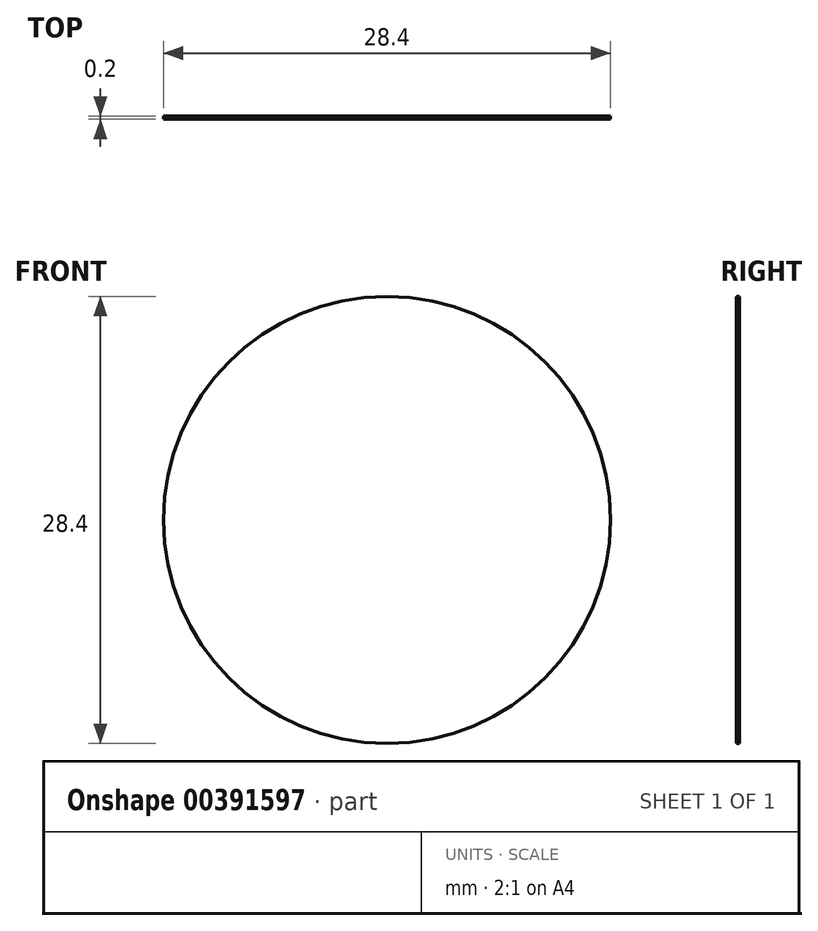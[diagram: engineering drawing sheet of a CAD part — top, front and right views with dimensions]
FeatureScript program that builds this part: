
annotation { "Feature Type Name" : "Feature", "Feature Type Description" : "" }
export const myFeature = defineFeature(function(context is Context, id is Id, definition is map)
    precondition{}
    {
        {
            var Q0;
            Q0=qCreatedBy(makeId("Front.planeOp"),FACE);
            var sketch = newSketch(context, id + "F0", { "sketchPlane" : qUnion([Q0])});
            skCircle(sketch, "E0", {"center": v(0, 0) * mm, "radius": 7 * mm, "construction": true});
            skCircle(sketch, "E1", {"center": v(0, 0) * mm, "radius": 10.5 * mm, "construction": true});
            skLineSegment(sketch, "E2", {"start": v(0, 7) * mm, "end": v(0.75, 7) * mm, "construction": true});
            skLineSegment(sketch, "E3", {"start": v(0.75, 7) * mm, "end": v(0.75, 13.5) * mm, "construction": true});
            skLineSegment(sketch, "E4", {"start": v(0.75, 13.5) * mm, "end": v(0, 13.5) * mm, "construction": true});
            skLineSegment(sketch, "E5", {"start": v(0, 13.5) * mm, "end": v(-0.75, 13.5) * mm, "construction": true});
            skLineSegment(sketch, "E6", {"start": v(-0.75, 13.5) * mm, "end": v(-0.75, 7) * mm, "construction": true});
            skLineSegment(sketch, "E7", {"start": v(-0.75, 7) * mm, "end": v(0, 7) * mm, "construction": true});
            skLineSegment(sketch, "E8.1.0", {"start": v(-2.85, 6.44) * mm, "end": v(-6.1, 12.07) * mm});
            skLineSegment(sketch, "E8.1.1", {"start": v(-7.4, 11.32) * mm, "end": v(-4.15, 5.69) * mm});
            skLineSegment(sketch, "E8.1.2", {"start": v(-4.15, 5.69) * mm, "end": v(-3.5, 6.06) * mm});
            skLineSegment(sketch, "E8.1.3", {"start": v(-3.5, 6.06) * mm, "end": v(-2.85, 6.44) * mm});
            skLineSegment(sketch, "E8.1.4", {"start": v(-6.1, 12.07) * mm, "end": v(-6.75, 11.7) * mm});
            skLineSegment(sketch, "E8.1.5", {"start": v(-6.75, 11.7) * mm, "end": v(-7.4, 11.32) * mm});
            skLineSegment(sketch, "E8.2.0", {"start": v(-5.69, 4.15) * mm, "end": v(-11.32, 7.4) * mm});
            skLineSegment(sketch, "E8.2.1", {"start": v(-12.07, 6.1) * mm, "end": v(-6.44, 2.85) * mm});
            skLineSegment(sketch, "E8.2.2", {"start": v(-6.44, 2.85) * mm, "end": v(-6.06, 3.5) * mm});
            skLineSegment(sketch, "E8.2.3", {"start": v(-6.06, 3.5) * mm, "end": v(-5.69, 4.15) * mm});
            skLineSegment(sketch, "E8.2.4", {"start": v(-11.32, 7.4) * mm, "end": v(-11.7, 6.75) * mm});
            skLineSegment(sketch, "E8.2.5", {"start": v(-11.7, 6.75) * mm, "end": v(-12.07, 6.1) * mm});
            skLineSegment(sketch, "E8.3.0", {"start": v(-7, 0.75) * mm, "end": v(-13.5, 0.75) * mm, "construction": true});
            skLineSegment(sketch, "E8.3.1", {"start": v(-13.5, -0.75) * mm, "end": v(-7, -0.75) * mm, "construction": true});
            skLineSegment(sketch, "E8.3.2", {"start": v(-7, -0.75) * mm, "end": v(-7, 0) * mm, "construction": true});
            skLineSegment(sketch, "E8.3.3", {"start": v(-7, 0) * mm, "end": v(-7, 0.75) * mm, "construction": true});
            skLineSegment(sketch, "E8.3.4", {"start": v(-13.5, 0.75) * mm, "end": v(-13.5, 0) * mm, "construction": true});
            skLineSegment(sketch, "E8.3.5", {"start": v(-13.5, 0) * mm, "end": v(-13.5, -0.75) * mm, "construction": true});
            skLineSegment(sketch, "E8.4.0", {"start": v(-6.44, -2.85) * mm, "end": v(-12.07, -6.1) * mm});
            skLineSegment(sketch, "E8.4.1", {"start": v(-11.32, -7.4) * mm, "end": v(-5.69, -4.15) * mm});
            skLineSegment(sketch, "E8.4.2", {"start": v(-5.69, -4.15) * mm, "end": v(-6.06, -3.5) * mm});
            skLineSegment(sketch, "E8.4.3", {"start": v(-6.06, -3.5) * mm, "end": v(-6.44, -2.85) * mm});
            skLineSegment(sketch, "E8.4.4", {"start": v(-12.07, -6.1) * mm, "end": v(-11.7, -6.75) * mm});
            skLineSegment(sketch, "E8.4.5", {"start": v(-11.7, -6.75) * mm, "end": v(-11.32, -7.4) * mm});
            skLineSegment(sketch, "E8.5.0", {"start": v(-4.15, -5.69) * mm, "end": v(-7.4, -11.32) * mm});
            skLineSegment(sketch, "E8.5.1", {"start": v(-6.1, -12.07) * mm, "end": v(-2.85, -6.44) * mm});
            skLineSegment(sketch, "E8.5.2", {"start": v(-2.85, -6.44) * mm, "end": v(-3.5, -6.06) * mm});
            skLineSegment(sketch, "E8.5.3", {"start": v(-3.5, -6.06) * mm, "end": v(-4.15, -5.69) * mm});
            skLineSegment(sketch, "E8.5.4", {"start": v(-7.4, -11.32) * mm, "end": v(-6.75, -11.7) * mm});
            skLineSegment(sketch, "E8.5.5", {"start": v(-6.75, -11.7) * mm, "end": v(-6.1, -12.07) * mm});
            skLineSegment(sketch, "E8.6.0", {"start": v(-0.75, -7) * mm, "end": v(-0.75, -13.5) * mm, "construction": true});
            skLineSegment(sketch, "E8.6.1", {"start": v(0.75, -13.5) * mm, "end": v(0.75, -7) * mm, "construction": true});
            skLineSegment(sketch, "E8.6.2", {"start": v(0.75, -7) * mm, "end": v(0, -7) * mm, "construction": true});
            skLineSegment(sketch, "E8.6.3", {"start": v(0, -7) * mm, "end": v(-0.75, -7) * mm, "construction": true});
            skLineSegment(sketch, "E8.6.4", {"start": v(-0.75, -13.5) * mm, "end": v(0, -13.5) * mm, "construction": true});
            skLineSegment(sketch, "E8.6.5", {"start": v(0, -13.5) * mm, "end": v(0.75, -13.5) * mm, "construction": true});
            skLineSegment(sketch, "E8.7.0", {"start": v(2.85, -6.44) * mm, "end": v(6.1, -12.07) * mm});
            skLineSegment(sketch, "E8.7.1", {"start": v(7.4, -11.32) * mm, "end": v(4.15, -5.69) * mm});
            skLineSegment(sketch, "E8.7.2", {"start": v(4.15, -5.69) * mm, "end": v(3.5, -6.06) * mm});
            skLineSegment(sketch, "E8.7.3", {"start": v(3.5, -6.06) * mm, "end": v(2.85, -6.44) * mm});
            skLineSegment(sketch, "E8.7.4", {"start": v(6.1, -12.07) * mm, "end": v(6.75, -11.7) * mm});
            skLineSegment(sketch, "E8.7.5", {"start": v(6.75, -11.7) * mm, "end": v(7.4, -11.32) * mm});
            skLineSegment(sketch, "E8.8.0", {"start": v(5.69, -4.15) * mm, "end": v(11.32, -7.4) * mm});
            skLineSegment(sketch, "E8.8.1", {"start": v(12.07, -6.1) * mm, "end": v(6.44, -2.85) * mm});
            skLineSegment(sketch, "E8.8.2", {"start": v(6.44, -2.85) * mm, "end": v(6.06, -3.5) * mm});
            skLineSegment(sketch, "E8.8.3", {"start": v(6.06, -3.5) * mm, "end": v(5.69, -4.15) * mm});
            skLineSegment(sketch, "E8.8.4", {"start": v(11.32, -7.4) * mm, "end": v(11.7, -6.75) * mm});
            skLineSegment(sketch, "E8.8.5", {"start": v(11.7, -6.75) * mm, "end": v(12.07, -6.1) * mm});
            skLineSegment(sketch, "E8.9.0", {"start": v(7, -0.75) * mm, "end": v(13.5, -0.75) * mm, "construction": true});
            skLineSegment(sketch, "E8.9.1", {"start": v(13.5, 0.75) * mm, "end": v(7, 0.75) * mm, "construction": true});
            skLineSegment(sketch, "E8.9.2", {"start": v(7, 0.75) * mm, "end": v(7, 0) * mm, "construction": true});
            skLineSegment(sketch, "E8.9.3", {"start": v(7, 0) * mm, "end": v(7, -0.75) * mm, "construction": true});
            skLineSegment(sketch, "E8.9.4", {"start": v(13.5, -0.75) * mm, "end": v(13.5, 0) * mm, "construction": true});
            skLineSegment(sketch, "E8.9.5", {"start": v(13.5, 0) * mm, "end": v(13.5, 0.75) * mm, "construction": true});
            skLineSegment(sketch, "E8.10.0", {"start": v(6.44, 2.85) * mm, "end": v(12.07, 6.1) * mm});
            skLineSegment(sketch, "E8.10.1", {"start": v(11.32, 7.4) * mm, "end": v(5.69, 4.15) * mm});
            skLineSegment(sketch, "E8.10.2", {"start": v(5.69, 4.15) * mm, "end": v(6.06, 3.5) * mm});
            skLineSegment(sketch, "E8.10.3", {"start": v(6.06, 3.5) * mm, "end": v(6.44, 2.85) * mm});
            skLineSegment(sketch, "E8.10.4", {"start": v(12.07, 6.1) * mm, "end": v(11.7, 6.75) * mm});
            skLineSegment(sketch, "E8.10.5", {"start": v(11.7, 6.75) * mm, "end": v(11.32, 7.4) * mm});
            skLineSegment(sketch, "E8.11.0", {"start": v(4.15, 5.69) * mm, "end": v(7.4, 11.32) * mm});
            skLineSegment(sketch, "E8.11.1", {"start": v(6.1, 12.07) * mm, "end": v(2.85, 6.44) * mm});
            skLineSegment(sketch, "E8.11.2", {"start": v(2.85, 6.44) * mm, "end": v(3.5, 6.06) * mm});
            skLineSegment(sketch, "E8.11.3", {"start": v(3.5, 6.06) * mm, "end": v(4.15, 5.69) * mm});
            skLineSegment(sketch, "E8.11.4", {"start": v(7.4, 11.32) * mm, "end": v(6.75, 11.7) * mm});
            skLineSegment(sketch, "E8.11.5", {"start": v(6.75, 11.7) * mm, "end": v(6.1, 12.07) * mm});
            skCircle(sketch, "E9", {"center": v(0, 0) * mm, "radius": 13.5 * mm, "construction": true});
            skSolve(sketch);
        }
        {
            var Q0;
            Q0=qCreatedBy(makeId("Front.planeOp"),FACE);
            var sketch = newSketch(context, id + "F1", { "sketchPlane" : qUnion([Q0])});
            skText(sketch, "E10", { "text": "12", "fontName": "AllertaStencil-Regular.ttf"});
            skText(sketch, "E11", { "text": "6", "fontName": "AllertaStencil-Regular.ttf"});
            skText(sketch, "E12", { "text": "9", "fontName": "AllertaStencil-Regular.ttf"});
            skPoint(sketch, "E13", {"position": v(-10.5, 0) * mm});
            skText(sketch, "E14", { "text": "3", "fontName": "AllertaStencil-Regular.ttf"});
            skCircle(sketch, "E15", {"center": v(0, 0) * mm, "radius": 10.5 * mm, "construction": true});
            skCircle(sketch, "E16", {"center": v(0, 0) * mm, "radius": 7 * mm, "construction": true});
            skLineSegment(sketch, "E17", {"start": v(0, 0) * mm, "end": v(0, 10.5) * mm, "construction": true});
            skLineSegment(sketch, "E18.1.0", {"start": v(0, 0) * mm, "end": v(-10.5, 0) * mm, "construction": true});
            skLineSegment(sketch, "E18.2.0", {"start": v(0, 0) * mm, "end": v(0, -10.5) * mm, "construction": true});
            skLineSegment(sketch, "E18.3.0", {"start": v(0, 0) * mm, "end": v(10.5, 0) * mm, "construction": true});
            skPoint(sketch, "E19", {"position": v(10.5, 0) * mm});
            const initialGuessF1  = {"E10": [-0.00246, 0.007, 1, 0, 0.0035], "E11": [-0.00153, -0.0105, 1, 0, 0.0035], "E12": [-0.0105, -0.00175, 1, 0, 0.0035], "E14": [0.00776, -0.00175, 1, 0, 0.0035]};
            skSetInitialGuess(sketch, initialGuessF1);
            skSolve(sketch);
        }
        {
            var Q0;
            Q0=qCreatedBy(makeId("Front.planeOp"),FACE);
            var sketch = newSketch(context, id + "F2", { "sketchPlane" : qUnion([Q0])});
            skCircle(sketch, "E20", {"center": v(0, 0) * mm, "radius": 14.2 * mm});
            skSolve(sketch);
        }
        {
            var Q0;
            Q0=qCreatedBy(makeId("Front.planeOp"),FACE);
            var sketch = newSketch(context, id + "F3", { "sketchPlane" : qUnion([Q0])});
            skCircle(sketch, "E21", {"center": v(0, 0) * mm, "radius": 12 * mm, "construction": true});
            skCircle(sketch, "E22", {"center": v(0, 0) * mm, "radius": 11 * mm, "construction": true});
            skCircle(sketch, "E23", {"center": v(0, 0) * mm, "radius": 13.5 * mm, "construction": true});
            skLineSegment(sketch, "E24", {"start": v(0, 0) * mm, "end": v(-11, 0) * mm, "construction": true});
            skLineSegment(sketch, "E25", {"start": v(-11, 0.73) * mm, "end": v(-13.5, 0.73) * mm});
            skLineSegment(sketch, "E26", {"start": v(-13.5, 0.73) * mm, "end": v(-13.5, -0.73) * mm});
            skLineSegment(sketch, "E27", {"start": v(-13.5, -0.73) * mm, "end": v(-11, -0.73) * mm});
            skLineSegment(sketch, "E28", {"start": v(-11, -0.73) * mm, "end": v(-11, 0) * mm});
            skLineSegment(sketch, "E29", {"start": v(-11, 0.73) * mm, "end": v(-11, 0) * mm});
            skLineSegment(sketch, "E30.1.0", {"start": v(0.73, -11) * mm, "end": v(0, -11) * mm});
            skLineSegment(sketch, "E30.1.1", {"start": v(-0.73, -11) * mm, "end": v(0, -11) * mm});
            skLineSegment(sketch, "E30.1.2", {"start": v(-0.73, -13.5) * mm, "end": v(0.73, -13.5) * mm});
            skLineSegment(sketch, "E30.1.3", {"start": v(-0.73, -11) * mm, "end": v(-0.73, -13.5) * mm});
            skLineSegment(sketch, "E30.1.4", {"start": v(0.73, -13.5) * mm, "end": v(0.73, -11) * mm});
            skLineSegment(sketch, "E30.2.0", {"start": v(11, 0.73) * mm, "end": v(11, 0) * mm});
            skLineSegment(sketch, "E30.2.1", {"start": v(11, -0.73) * mm, "end": v(11, 0) * mm});
            skLineSegment(sketch, "E30.2.2", {"start": v(13.5, -0.73) * mm, "end": v(13.5, 0.73) * mm});
            skLineSegment(sketch, "E30.2.3", {"start": v(11, -0.73) * mm, "end": v(13.5, -0.73) * mm});
            skLineSegment(sketch, "E30.2.4", {"start": v(13.5, 0.73) * mm, "end": v(11, 0.73) * mm});
            skLineSegment(sketch, "E30.3.0", {"start": v(-0.73, 11) * mm, "end": v(0, 11) * mm});
            skLineSegment(sketch, "E30.3.1", {"start": v(0.73, 11) * mm, "end": v(0, 11) * mm});
            skLineSegment(sketch, "E30.3.2", {"start": v(0.73, 13.5) * mm, "end": v(-0.73, 13.5) * mm});
            skLineSegment(sketch, "E30.3.3", {"start": v(0.73, 11) * mm, "end": v(0.73, 13.5) * mm});
            skLineSegment(sketch, "E30.3.4", {"start": v(-0.73, 13.5) * mm, "end": v(-0.73, 11) * mm});
            skSolve(sketch);
        }
        {
            var Q0;
            Q0=qSketchRegion(id+"F2",true);
            extrude(context, id + "F4", {"entities" : qUnion([Q0]), "depth" : 0.2 * mm});
        }
    });
